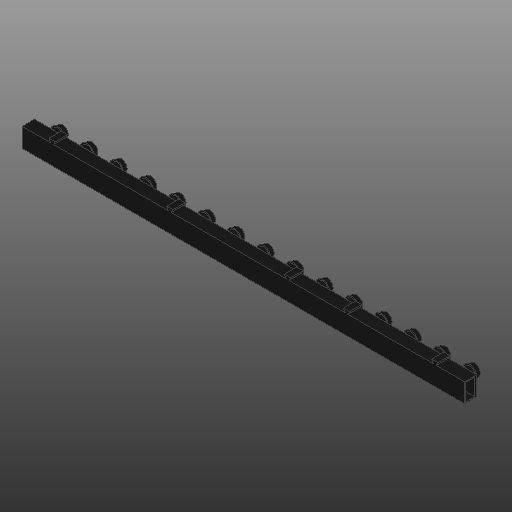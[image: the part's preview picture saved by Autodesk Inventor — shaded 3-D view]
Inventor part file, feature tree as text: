
AUTODESK INVENTOR PART (.ipt)
format: ipt  version: 2020 (Build 240168000, 168)  size: 280,576 bytes
history: native  units: in
note: dims shown in document units (in); Inventor stores cm internally (conversion verified against a paired STEP export)
features: other x6, extrude x3, pattern_linear x1, projected_geometry x1
ambient origin geometry x8: Origin, YZ Plane, XZ Plane, XY Plane, X Axis, Y Axis, Z Axis, Center Point
bodies: Solid1 (feature_tree)
feature tree (11):
  extrude  "Box"  Depth=0.0315in
  other  "Fitting Plane"
  other  "Fitting"
  extrude  "Fitting Entrance"  Depth=0.0157in
  pattern_linear  "Channel Repetition"  Spacing1=0.0157in  [1 undecoded]
  extrude  "Tabs"  Depth=0.4882in TaperAngle=0.0deg
  other  "Box Sketch"
  other  "Fitting Sketch"
  other  "Fitting Entrance Sketch"
  projected_geometry  "Projected Loop1"
  other  "Tab Sketch"
note: 1 required parameter value undecoded (feature->parameter linkage not recoverable at this tier; creation-order binding heuristic only, values carry confidence <= 0.55)
